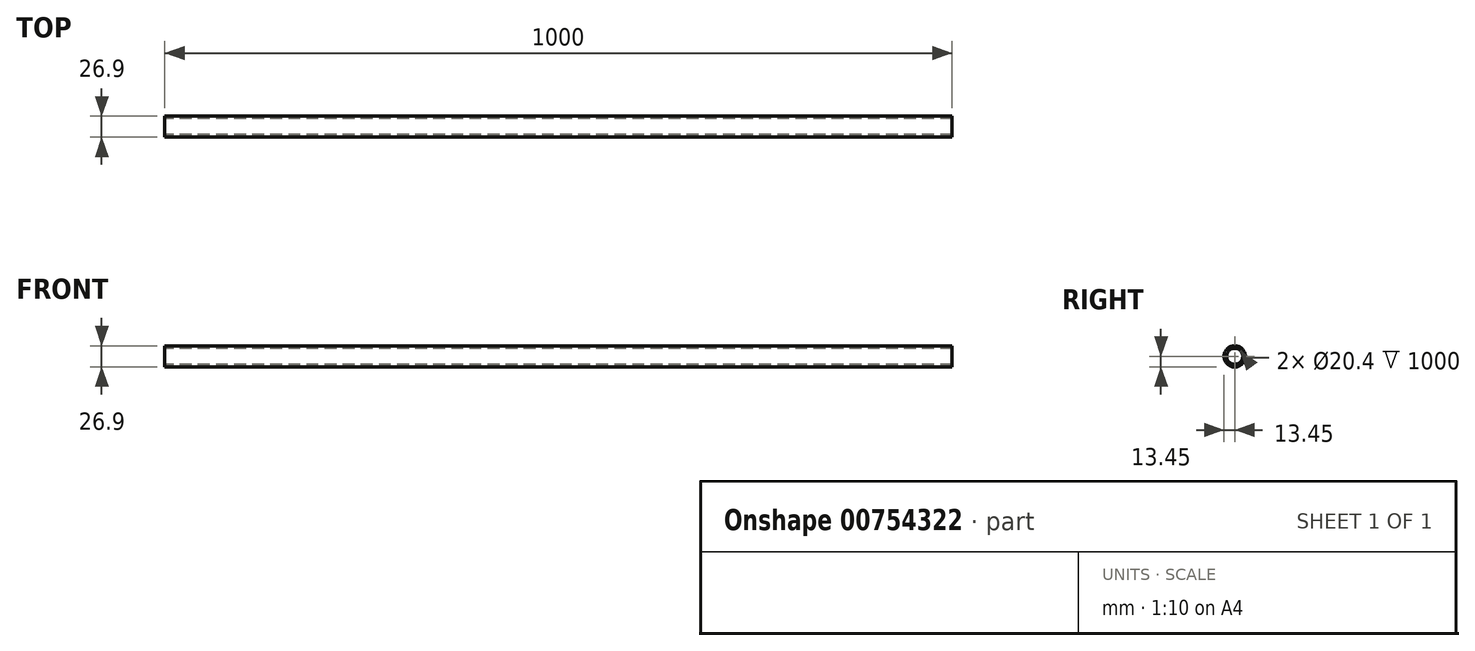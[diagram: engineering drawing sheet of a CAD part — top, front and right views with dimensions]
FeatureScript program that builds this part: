
annotation { "Feature Type Name" : "Feature", "Feature Type Description" : "" }
export const myFeature = defineFeature(function(context is Context, id is Id, definition is map)
    precondition{}
    {
        {
            var Q0;
            Q0=qCreatedBy(makeId("Right.planeOp"),FACE);
            var sketch = newSketch(context, id + "F0", { "sketchPlane" : qUnion([Q0])});
            skCircle(sketch, "E0", {"center": v(0, 0) * mm, "radius": 13.45 * mm});
            skCircle(sketch, "E1", {"center": v(0, 0) * mm, "radius": 10.2 * mm});
            skSolve(sketch);
        }
        {
            var Q0;
            Q0=makeQuery(id+"F0.imprint","IMPRINT",FACE,{"disambiguationData":[TD([[makeQuery(id+"F0.imprint","IMPRINT",EDGE,{"derivedFrom":sQuery(id+"F0.wireOp",EDGE,"E0")}),1.0]])]});
            extrude(context, id + "F1", {"entities" : qUnion([Q0]), "depth" : 1000 * mm, "offsetDistance" : 25 * mm});
        }
    });
